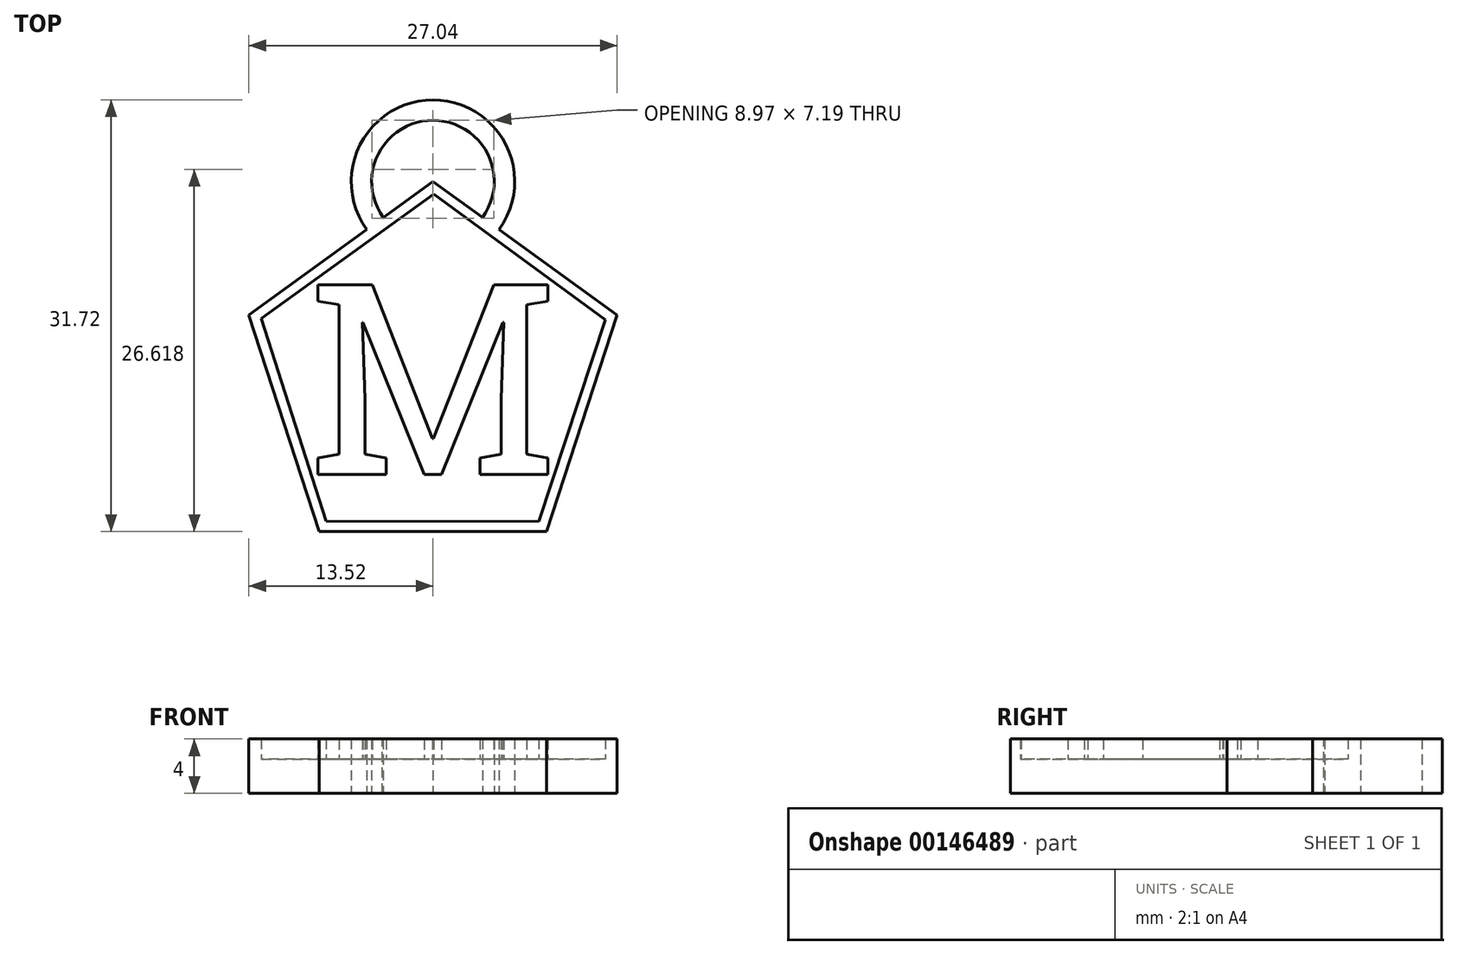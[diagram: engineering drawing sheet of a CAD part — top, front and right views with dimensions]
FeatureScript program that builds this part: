
annotation { "Feature Type Name" : "Feature", "Feature Type Description" : "" }
export const myFeature = defineFeature(function(context is Context, id is Id, definition is map)
    precondition{}
    {
        {
            var Q0;
            Q0=qCreatedBy(makeId("Top.planeOp"),FACE);
            var sketch = newSketch(context, id + "F0", { "sketchPlane" : qUnion([Q0])});
            skCircle(sketch, "E0.cCircle", {"center": v(-26.08, 11.5) * mm, "radius": 11.5 * mm, "construction": true});
            skLineSegment(sketch, "E0.0", {"start": v(-12.56, 15.9) * mm, "end": v(-17.72, 0) * mm});
            skLineSegment(sketch, "E0.1", {"start": v(-17.72, 0) * mm, "end": v(-34.43, 0) * mm});
            skLineSegment(sketch, "E0.2", {"start": v(-34.43, 0) * mm, "end": v(-39.6, 15.9) * mm});
            skLineSegment(sketch, "E0.3", {"start": v(-39.6, 15.9) * mm, "end": v(-26.08, 25.71) * mm});
            skLineSegment(sketch, "E0.4", {"start": v(-26.08, 25.71) * mm, "end": v(-12.56, 15.9) * mm});
            skPoint(sketch, "E0.0.midPoint", {"position": v(-15.14, 7.95) * mm});
            skCircle(sketch, "E1.cCircle", {"center": v(-26.08, 11.5) * mm, "radius": 10.75 * mm, "construction": true});
            skLineSegment(sketch, "E1.0", {"start": v(-13.43, 15.57) * mm, "end": v(-18.3, 0.73) * mm});
            skLineSegment(sketch, "E1.1", {"start": v(-18.3, 0.73) * mm, "end": v(-33.92, 0.77) * mm});
            skLineSegment(sketch, "E1.2", {"start": v(-33.92, 0.77) * mm, "end": v(-38.7, 15.65) * mm});
            skLineSegment(sketch, "E1.3", {"start": v(-38.7, 15.65) * mm, "end": v(-26.04, 24.79) * mm});
            skLineSegment(sketch, "E1.4", {"start": v(-26.04, 24.79) * mm, "end": v(-13.43, 15.57) * mm});
            skPoint(sketch, "E1.0.midPoint", {"position": v(-15.87, 8.15) * mm});
            skSolve(sketch);
        }
        {
            var Q0;
            Q0=makeQuery(id+"F0.imprint","IMPRINT",FACE,{"disambiguationData":[TD([[makeQuery(id+"F0.imprint","IMPRINT",EDGE,{"derivedFrom":sQuery(id+"F0.wireOp",EDGE,"E0.0")}),-1.0]])]});
            extrude(context, id + "F1", {"entities" : qUnion([Q0]), "depth" : 2 * mm});
        }
        {
            var Q0;
            Q0=makeQuery(id+"F0.imprint","IMPRINT",FACE,{"disambiguationData":[TD([[makeQuery(id+"F0.imprint","IMPRINT",EDGE,{"derivedFrom":sQuery(id+"F0.wireOp",EDGE,"E1.0")}),-1.0]])]});
            extrude(context, id + "F2", {"entities" : qUnion([Q0]), "operationType" : NewBodyOperationType.ADD, "depth" : 0.5 * mm});
        }
        {
            var Q0;
            Q0=makeQuery(id+"F0.imprint","IMPRINT",FACE,{"disambiguationData":[TD([[makeQuery(id+"F0.imprint","IMPRINT",EDGE,{"derivedFrom":sQuery(id+"F0.wireOp",EDGE,"E0.0")}),-1.0]])]});
            extrude(context, id + "F3", {"entities" : qUnion([Q0]), "operationType" : NewBodyOperationType.ADD, "oppositeDirection" : true, "depth" : 2 * mm});
        }
        {
            var Q0;
            Q0=makeQuery(id+"F0.imprint","IMPRINT",FACE,{"disambiguationData":[TD([[makeQuery(id+"F0.imprint","IMPRINT",EDGE,{"derivedFrom":sQuery(id+"F0.wireOp",EDGE,"E1.0")}),-1.0]])]});
            extrude(context, id + "F4", {"entities" : qUnion([Q0]), "operationType" : NewBodyOperationType.ADD, "oppositeDirection" : true, "depth" : 0.5 * mm});
        }
        {
            var Q0;
            Q0=qCreatedBy(makeId("Top.planeOp"),FACE);
            var sketch = newSketch(context, id + "F5", { "sketchPlane" : qUnion([Q0])});
            skText(sketch, "E2", { "text": "M", "fontName": "RobotoSlab-Regular.ttf"});
            const initialGuessF5  = {"E2": [-0.03546, 0.0039, 1, 0, 0.014]};
            skSetInitialGuess(sketch, initialGuessF5);
            skSolve(sketch);
        }
        {
            var Q0;
            Q0=makeQuery(id+"F2.opExtrude","CAP_FACE",FACE,{"disambiguationData":[OSD([sQuery(id+"F0.wireOp",EDGE,"E1.0"),sQuery(id+"F0.wireOp",EDGE,"E1.1"),sQuery(id+"F0.wireOp",EDGE,"E1.2"),sQuery(id+"F0.wireOp",EDGE,"E1.3"),sQuery(id+"F0.wireOp",EDGE,"E1.4")])],"isStart":false});
            var sketch = newSketch(context, id + "F6", { "sketchPlane" : qUnion([Q0])});
            skText(sketch, "E3", { "text": "M", "fontName": "RobotoSlab-Regular.ttf"});
            const initialGuessF6  = {"E3": [-0.0352, 0.0042, 1, 0, 0.01412]};
            skSetInitialGuess(sketch, initialGuessF6);
            skSolve(sketch);
        }
        {
            var Q0;
            Q0 = qSketchRegion(id + "F6", true);
            extrude(context, id + "F7", {"entities" : qUnion([Q0]), "operationType" : NewBodyOperationType.ADD, "depth" : 1.47 * mm});
        }
        {
            var Q0;
            Q0=qCreatedBy(makeId("Top.planeOp"),FACE);
            var sketch = newSketch(context, id + "F8", { "sketchPlane" : qUnion([Q0])});
            skArc(sketch, "E4", {"start": v(-26.02, 31.71) * mm, "mid": v(-31.48, 28.32) * mm, "end": v(-30.74, 21.93) * mm});
            skArc(sketch, "E5", {"start": v(-26.02, 31.71) * mm, "mid": v(-20.65, 28.27) * mm, "end": v(-21.41, 21.94) * mm});
            skArc(sketch, "E6", {"start": v(-22.45, 23.06) * mm, "mid": v(-26.06, 30.21) * mm, "end": v(-29.73, 23.08) * mm});
            skLineSegment(sketch, "E7", {"start": v(-30.74, 21.93) * mm, "end": v(-29.73, 23.08) * mm});
            skLineSegment(sketch, "E8", {"start": v(-21.41, 21.94) * mm, "end": v(-22.45, 23.06) * mm});
            skSolve(sketch);
        }
        {
            var Q0;
            Q0=makeQuery(id+"F8.imprint","IMPRINT",FACE,{"disambiguationData":[TD([[makeQuery(id+"F8.imprint","IMPRINT",EDGE,{"derivedFrom":sQuery(id+"F8.wireOp",EDGE,"E4")}),1.0]])]});
            extrude(context, id + "F9", {"entities" : qUnion([Q0]), "operationType" : NewBodyOperationType.ADD, "depth" : 2 * mm});
        }
        {
            var Q0;
            Q0=makeQuery(id+"F9.opExtrude","CAP_FACE",FACE,{"disambiguationData":[OSD([sQuery(id+"F8.wireOp",EDGE,"E4"),sQuery(id+"F8.wireOp",EDGE,"E5"),sQuery(id+"F8.wireOp",EDGE,"E6"),sQuery(id+"F8.wireOp",EDGE,"E7"),sQuery(id+"F8.wireOp",EDGE,"E8")])],"isStart":true});
            extrude(context, id + "F10", {"entities" : qUnion([Q0]), "operationType" : NewBodyOperationType.ADD, "depth" : 2 * mm});
        }
        {
            var Q0;
            Q0=makeQuery(id+"F4.opExtrude","CAP_FACE",FACE,{"disambiguationData":[OSD([sQuery(id+"F0.wireOp",EDGE,"E1.0"),sQuery(id+"F0.wireOp",EDGE,"E1.1"),sQuery(id+"F0.wireOp",EDGE,"E1.2"),sQuery(id+"F0.wireOp",EDGE,"E1.3"),sQuery(id+"F0.wireOp",EDGE,"E1.4")])],"isStart":false});
            extrude(context, id + "F11", {"entities" : qUnion([Q0]), "operationType" : NewBodyOperationType.ADD, "depth" : 1.5 * mm});
        }
    });
